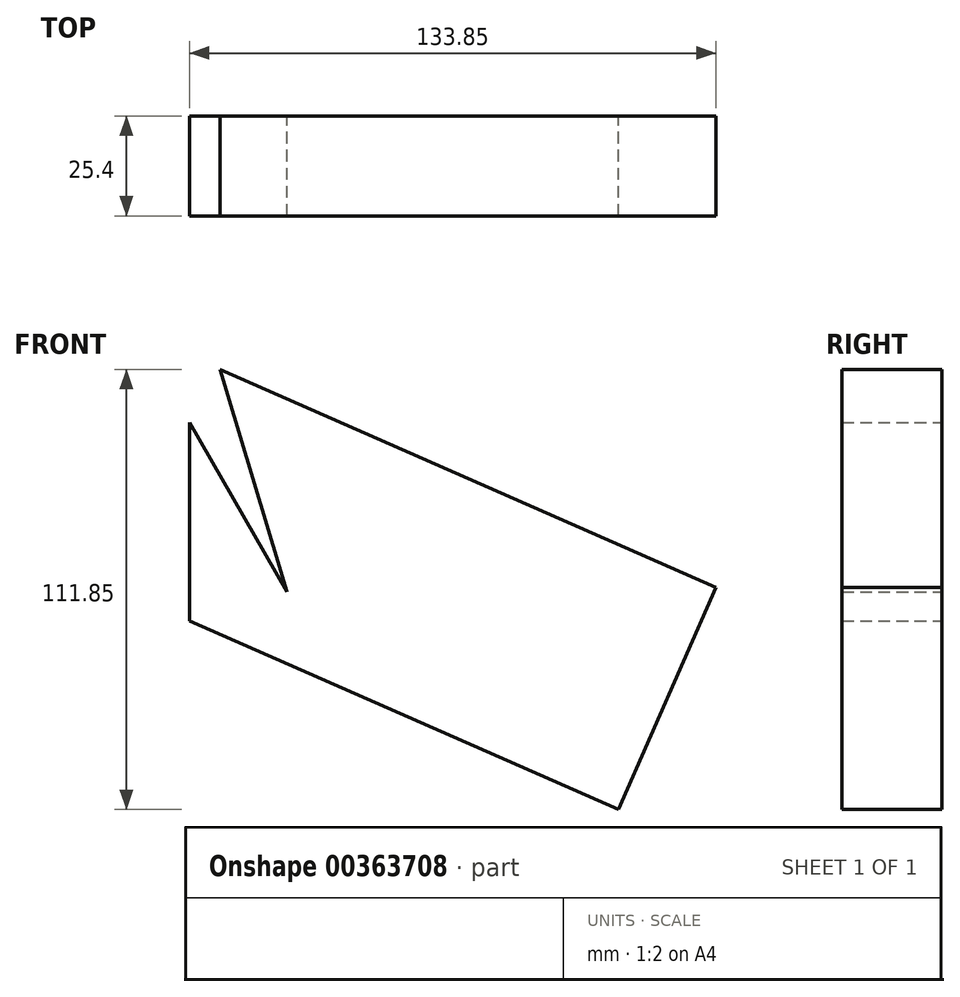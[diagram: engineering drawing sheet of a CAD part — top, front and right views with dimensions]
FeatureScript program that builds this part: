
annotation { "Feature Type Name" : "Feature", "Feature Type Description" : "" }
export const myFeature = defineFeature(function(context is Context, id is Id, definition is map)
    precondition{}
    {
        {
            var Q0;
            Q0=qCreatedBy(makeId("Front.planeOp"),FACE);
            var sketch = newSketch(context, id + "F0", { "sketchPlane" : qUnion([Q0])});
            skLineSegment(sketch, "E0", {"start": v(-16.96, 56.53) * mm, "end": v(109.03, 1.06) * mm});
            skLineSegment(sketch, "E1", {"start": v(109.03, 1.06) * mm, "end": v(84.2, -55.32) * mm});
            skLineSegment(sketch, "E2", {"start": v(84.2, -55.32) * mm, "end": v(-24.82, -7.32) * mm});
            skLineSegment(sketch, "E3", {"start": v(-24.82, -7.32) * mm, "end": v(-24.82, 43) * mm});
            skLineSegment(sketch, "E4", {"start": v(-24.82, 43) * mm, "end": v(0, 0) * mm});
            skLineSegment(sketch, "E5", {"start": v(0, 0) * mm, "end": v(-16.96, 56.53) * mm});
            skSolve(sketch);
        }
        {
            var Q0;
            Q0 = qSketchRegion(id + "F0", true);
            extrude(context, id + "F1", {"entities" : qUnion([Q0]), "depth" : 25.4 * mm});
        }
    });
